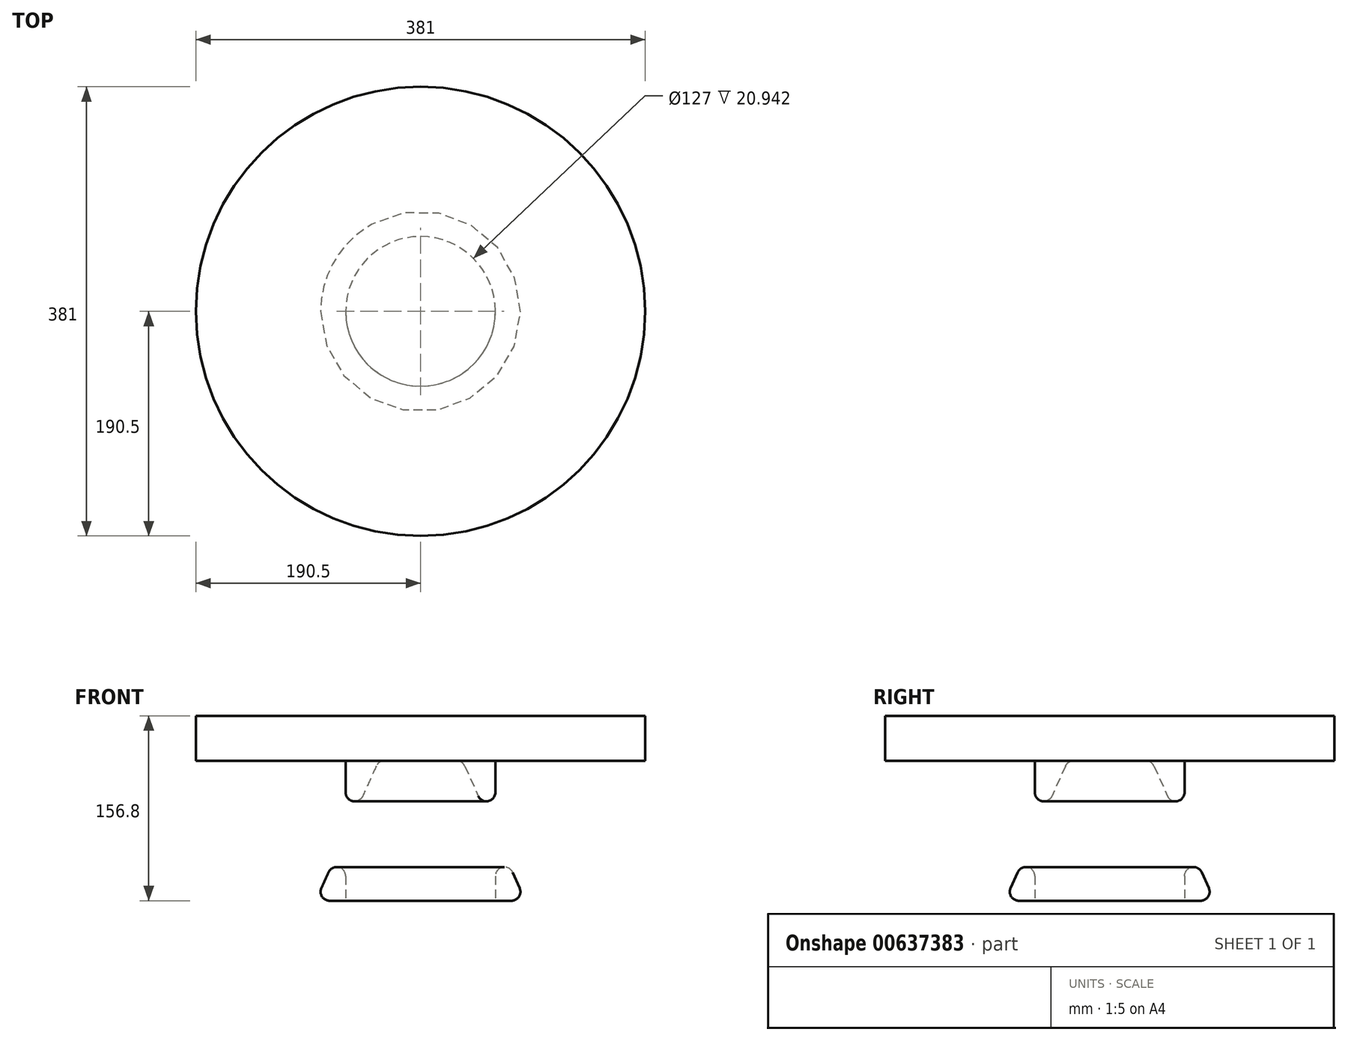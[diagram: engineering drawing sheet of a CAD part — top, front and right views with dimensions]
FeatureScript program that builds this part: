
annotation { "Feature Type Name" : "Feature", "Feature Type Description" : "" }
export const myFeature = defineFeature(function(context is Context, id is Id, definition is map)
    precondition{}
    {
        {
            var Q0;
            Q0=qCreatedBy(makeId("Right.planeOp"),FACE);
            var sketch = newSketch(context, id + "F0", { "sketchPlane" : qUnion([Q0])});
            skLineSegment(sketch, "E0", {"start": v(0, 0) * mm, "end": v(190.5, 0) * mm});
            skLineSegment(sketch, "E1", {"start": v(190.5, 0) * mm, "end": v(190.5, 38.1) * mm});
            skLineSegment(sketch, "E2", {"start": v(190.5, 38.1) * mm, "end": v(0, 38.1) * mm});
            skLineSegment(sketch, "E3", {"start": v(0, 38.1) * mm, "end": v(0, 0) * mm});
            skLineSegment(sketch, "E4", {"start": v(0, 38.1) * mm, "end": v(63.5, 38.1) * mm});
            skLineSegment(sketch, "E5", {"start": v(63.5, -118.7) * mm, "end": v(63.5, 38.1) * mm});
            skLineSegment(sketch, "E6", {"start": v(0, 0) * mm, "end": v(0, 8.3) * mm});
            skLineSegment(sketch, "E7", {"start": v(0, 8.3) * mm, "end": v(31.75, 8.3) * mm});
            skLineSegment(sketch, "E8", {"start": v(63.5, -118.7) * mm, "end": v(88.9, -118.7) * mm});
            skLineSegment(sketch, "E9", {"start": v(31.75, 8.3) * mm, "end": v(88.9, -118.7) * mm});
            skSolve(sketch);
        }
        {
            var Q0;
            Q0 = qSketchRegion(id + "F0", true);
            var Q1;
            Q1=sQuery(id+"F0.wireOp",EDGE,"E6");
            revolve(context, id + "F1", {"entities" : qUnion([Q0]), "axis" : qUnion([Q1]), "revolveType" : RevolveType.FULL});
        }
        {
            var Q0;
            Q0=makeQuery(id+"F1.opRevolve","SWEPT_EDGE",EDGE,{"disambiguationData":[OSD([sQuery(id+"F0.wireOp",EDGE,"E8"),sQuery(id+"F0.wireOp",EDGE,"E9")])]});
            var Q1;
            Q1=makeQuery(id+"F1.opRevolve","SWEPT_EDGE",EDGE,{"disambiguationData":[OSD([sQuery(id+"F0.wireOp",EDGE,"E7"),sQuery(id+"F0.wireOp",EDGE,"E9")])]});
            fillet(context, id + "F2", {"entities" : qUnion([Q0, Q1]), "radius" : 7.62 * mm, "tangentPropagation" : true, "allowEdgeOverflow" : false});
        }
    });
